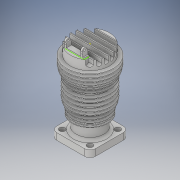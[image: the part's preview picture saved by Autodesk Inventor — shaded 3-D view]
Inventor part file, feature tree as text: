
AUTODESK INVENTOR PART (.ipt)
format: ipt  version: 2018 (Build 220112000, 112)  size: 665,088 bytes
history: native  units: in
note: dims shown in document units (in); Inventor stores cm internally (conversion verified against a paired STEP export)
features: sketch x8, extrude x5, fillet x4, revolve x3, other x1, pattern_linear x1, mirror x1
ambient origin geometry x8: Origin, YZ Plane, XZ Plane, XY Plane, X Axis, Y Axis, Z Axis, Center Point
bodies: Solid1 (feature_tree)
feature tree (23):
  extrude  "Extrusion1"  Depth=0.4724in
  fillet  "Fillet1"  Radius=0.4724in
  extrude  "Extrusion2"  Depth=0.3937in
  revolve  "Revolution1"  [1 undecoded]
  fillet  "Fillet2"  Radius=1.378in
  fillet  "Fillet3"  Radius=0.7874in
  sketch  "Sketch6"  dims[d17=90.0deg d18=0.1575in]
  other  "Work Axis1"
  revolve  "Revolution2"  [1 undecoded]
  revolve  "Revolution3"  [1 undecoded]
  extrude  "Extrusion3"  Depth=0.0197in
  pattern_linear  "Rectangular Pattern1"  Spacing1=0.0197in  [1 undecoded]
  fillet  "Fillet4"  Radius=0.0197in
  extrude  "Extrusion4"  Depth=0.0197in
  extrude  "Extrusion5"  Depth=0.0197in
  mirror  "Mirror1"
  sketch  "Sketch3"  dims[d0=2.7559in d1=2.7559in d2=0.4724in d3=0.0in]
  sketch  "Sketch4"  dims[d4=0.3937in d5=0.3937in]
  sketch  "Sketch5"  dims[d6=0.7874in d7=0.0in d14=1.378in d15=1.378in d16=0.7874in]
  sketch  "Sketch7"  dims[d19=0.1575in d20=0.7874in]
  sketch  "Sketch8"  dims[d21=0.1969in d24=0.0197in]
  sketch  "Sketch9"  dims[d26=0.2756in]
  sketch  "Sketch10"  dims[d28=0.0197in d29=0.2756in d30=0.0197in d31=0.2756in d32=0.0197in d33=0.2756in d34=0.0197in d35=0.2756in d36=0.0197in d37=0.2756in d38=0.0197in d39=0.2756in d40=0.0197in d41=0.2756in d42=0.0197in d43=0.2756in d44=0.0197in d45=0.2756in d46=0.0197in d47=0.2756in d48=0.0197in d49=0.2756in d50=0.0197in d51=0.2756in d52=0.0197in d53=0.2756in d54=0.0197in d55=0.2756in d56=0.0197in d57=0.2756in d58=90.0deg d59=90.0deg d60=0.9843in d61=0.3937in d62=1.1811in d63=3.937in d64=0.0in d65=2.3622in d67=0.3937in d68=0.0394in d69=0.0787in d70=0.0in d71=0.4724in d72=0.0in d73=0.1969in d74=0.1378in d75=0.1575in d76=0.1181in d77=0.0in]
note: 4 required parameter values undecoded (feature->parameter linkage not recoverable at this tier; creation-order binding heuristic only, values carry confidence <= 0.55)